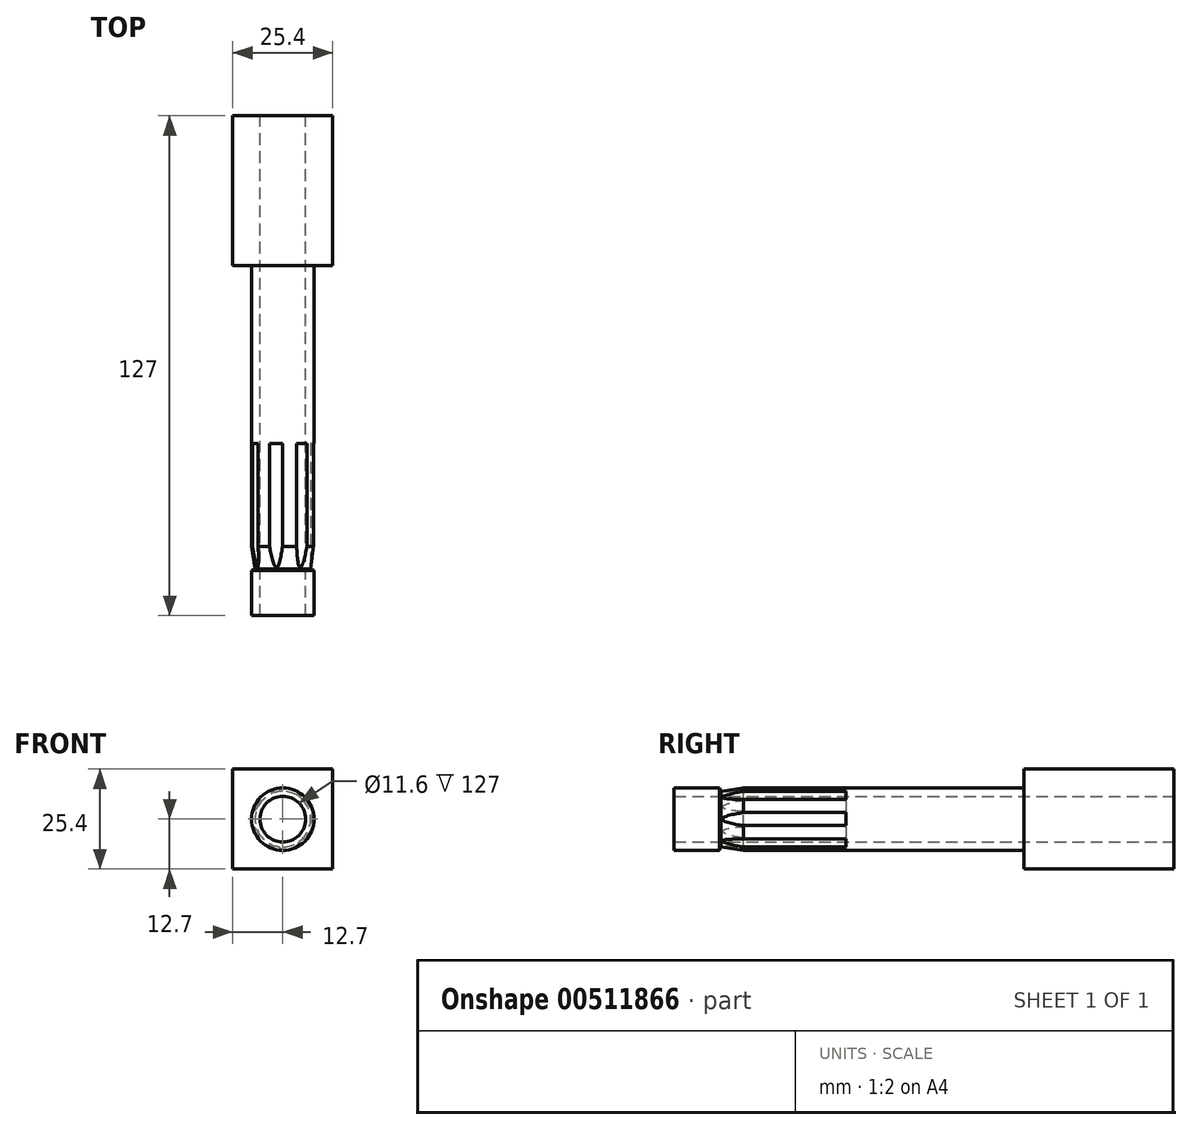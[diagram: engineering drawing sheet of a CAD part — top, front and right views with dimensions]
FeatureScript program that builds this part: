
annotation { "Feature Type Name" : "Feature", "Feature Type Description" : "" }
export const myFeature = defineFeature(function(context is Context, id is Id, definition is map)
    precondition{}
    {
        {
            var Q0;
            Q0=qCreatedBy(makeId("Front.planeOp"),FACE);
            var sketch = newSketch(context, id + "F0", { "sketchPlane" : qUnion([Q0])});
            skLineSegment(sketch, "E0.bottom", {"start": v(12.7, -12.7) * mm, "end": v(-12.7, -12.7) * mm});
            skLineSegment(sketch, "E0.top", {"start": v(12.7, 12.7) * mm, "end": v(-12.7, 12.7) * mm});
            skLineSegment(sketch, "E0.left", {"start": v(12.7, -12.7) * mm, "end": v(12.7, 12.7) * mm});
            skLineSegment(sketch, "E0.right", {"start": v(-12.7, -12.7) * mm, "end": v(-12.7, 12.7) * mm});
            skPoint(sketch, "E0.middle", {"position": v(0, 0) * mm});
            skCircle(sketch, "E1", {"center": v(0, 0) * mm, "radius": 7.94 * mm});
            skCircle(sketch, "E2", {"center": v(0, 0) * mm, "radius": 5.8 * mm});
            skSolve(sketch);
        }
        {
            var Q0;
            Q0=qSketchRegion(id+"F0",true);
            var Q1;
            Q1=makeQuery(id+"F0.imprint","IMPRINT",FACE,{"disambiguationData":[TD([[makeQuery(id+"F0.imprint","IMPRINT",EDGE,{"derivedFrom":sQuery(id+"F0.wireOp",EDGE,"E1")}),1.0]])]});
            extrude(context, id + "F1", {"entities" : qUnion([Q0, Q1]), "depth" : 38.1 * mm});
        }
        {
            var Q0;
            Q0=makeQuery(id+"F0.imprint","IMPRINT",FACE,{"disambiguationData":[TD([[makeQuery(id+"F0.imprint","IMPRINT",EDGE,{"derivedFrom":sQuery(id+"F0.wireOp",EDGE,"E1")}),1.0]])]});
            extrude(context, id + "F2", {"entities" : qUnion([Q0]), "operationType" : NewBodyOperationType.ADD, "depth" : 127 * mm, "offsetDistance" : 25.4 * mm});
        }
        {
            var Q0;
            Q0=qCreatedBy(makeId("Top.planeOp"),FACE);
            var sketch = newSketch(context, id + "F3", { "sketchPlane" : qUnion([Q0])});
            skLineSegment(sketch, "E3", {"start": v(-8.1, -115.62) * mm, "end": v(-7.07, -115.1) * mm});
            skLineSegment(sketch, "E4", {"start": v(-7.07, -115.1) * mm, "end": v(-8.03, -108.82) * mm});
            skLineSegment(sketch, "E5", {"start": v(-8.03, -108.82) * mm, "end": v(-8.1, -115.62) * mm});
            skLineSegment(sketch, "E6.direction1", {"start": v(-8.1, -115.62) * mm, "end": v(-0.22, -115.62) * mm, "construction": true});
            skLineSegment(sketch, "E6.direction2", {"start": v(-8.1, -115.62) * mm, "end": v(-8.1, -108.5) * mm, "construction": true});
            skSolve(sketch);
        }
        {
            var Q0;
            Q0=qSketchRegion(id+"F3",true);
            var Q1;
            Q1=makeQuery(id+"F1.opExtrude","CAP_EDGE",EDGE,{"disambiguationData":[OSD([sQuery(id+"F0.wireOp",EDGE,"E2")])],"isStart":true});
            revolve(context, id + "F4", {"operationType" : NewBodyOperationType.REMOVE, "entities" : qUnion([Q0]), "axis" : qUnion([Q1]), "revolveType" : RevolveType.FULL, "oppositeDirection" : true});
        }
        {
            var Q0;
            Q0=makeQuery(id+"F2.opExtrude","CAP_FACE",FACE,{"disambiguationData":[OSD([sQuery(id+"F0.wireOp",EDGE,"E1"),sQuery(id+"F0.wireOp",EDGE,"E2")])],"isStart":false});
            var sketch = newSketch(context, id + "F5", { "sketchPlane" : qUnion([Q0])});
            skCircle(sketch, "E7", {"center": v(9.58, 0) * mm, "radius": 2.46 * mm});
            skCircle(sketch, "E8.1.0", {"center": v(5.97, 7.49) * mm, "radius": 2.46 * mm});
            skCircle(sketch, "E8.2.0", {"center": v(-2.13, 9.34) * mm, "radius": 2.46 * mm});
            skCircle(sketch, "E8.3.0", {"center": v(-8.63, 4.16) * mm, "radius": 2.46 * mm});
            skCircle(sketch, "E8.4.0", {"center": v(-8.63, -4.16) * mm, "radius": 2.46 * mm});
            skCircle(sketch, "E8.5.0", {"center": v(-2.13, -9.34) * mm, "radius": 2.46 * mm});
            skCircle(sketch, "E8.6.0", {"center": v(5.97, -7.49) * mm, "radius": 2.46 * mm});
            skPoint(sketch, "E8.center", {"position": v(0, 0) * mm});
            skSolve(sketch);
        }
        {
            var Q0;
            Q0 = qSketchRegion(id + "F5", true);
            extrude(context, id + "F6", {"entities" : qUnion([Q0]), "operationType" : NewBodyOperationType.REMOVE, "oppositeDirection" : true, "depth" : 43.69 * mm, "offsetDistance" : 25.4 * mm, "hasSecondDirection" : true, "secondDirectionOppositeDirection" : true, "secondDirectionDepth" : 12.2 * mm});
        }
    });
